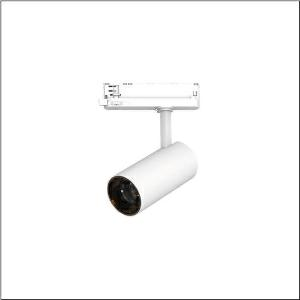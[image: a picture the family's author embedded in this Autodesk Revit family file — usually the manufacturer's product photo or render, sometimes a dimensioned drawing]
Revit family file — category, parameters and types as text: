
# Revit family: spot_31_slim_51sf127fb2b
name_source: partatom
category: Lighting Fixtures
units: mm (PartAtom-declared; Revit-internal decimal feet)

## family parameters
Cut with Voids When Loaded = No
Host = Face
Light Source = No
Part Type = Normal
Room Calculation Point = No
Round Connector Dimension = Use Diameter
Shared = No

## types (1)
- Spot 31 Slim (1 x LED, 1970 lm, 16.2 W, 3000K)
    Apparent Load = 16 VA
    CIE Flux Codes = 94 98 99 100 100
    Color Rendering = 90
    Color Temperature = 3000K
    Default Elevation = 1800 mm
    Description = Spot 31 Slim, directional spotlight, light control with reflector, of aluminium, LED rated luminous flux: 2.150lm, light colour: 930, control gear: ECG, with 3-phase adapter, mains connection: 220..240V, AC, 50/60Hz, housing, of aluminium, traffic white (RAL 9016), diameter: 70mm, adapter, of plastic, protection rating (complete): IP20, insulation class (complete): insulation class I (protective earthing), certification: CE, impact resistance: IK02, packaging unit: 1 piece
    Height = 210 mm
    Lamp = 1 x LED
    Lamp Light Flux = 1970 lm
    Lamp Power = 16.2 W
    Lamp count = 1
    Length = 70 mm
    Luminous efficacy = 122 lm/W
    Manufacturer = Siteco
    ModVariant = No
    Model = 51SF127FB2B
    Mounting Place = Ceiling
    Mounting Type = Pendant
    Number of Poles = 1
    OnlyDefault = Yes
    Power Factor = 1
    Product Name = Spot 31 Slim
    Product group = directional spotlight
    ProductGroupID = 905
    Protection Class = Protection class I
    Protection Degree = IP 20
    RLX_Detail_Level = 1
    RLX_Emergency_Light_Flux = 0 lm
    RLX_Emergency_Type = 0
    RLX_Emergency_Type_DB = No
    RlxData = <blob elided: 14165 chars, md5=ddc88921>
    Socket = socket
    Standby Power = 0 W
    System Light Flux = 1970 lm
    System Power = 16 W
    Type Comments = Product without accessories
    Type Image = l_1228468.jpg
    URL = http://relux.com
    VarID = ---
    Voltage = 0 V
    Weight = 0.00 kg
    Width = 0 mm  [stored 0 ft]

note: [stored X ft] marks values corroborated as IEEE doubles in the binary element streams (Revit-internal decimal feet)

## geometry (parser evidence)
native form markers: Sweep x9
no freeform markers — native parametric forms only
